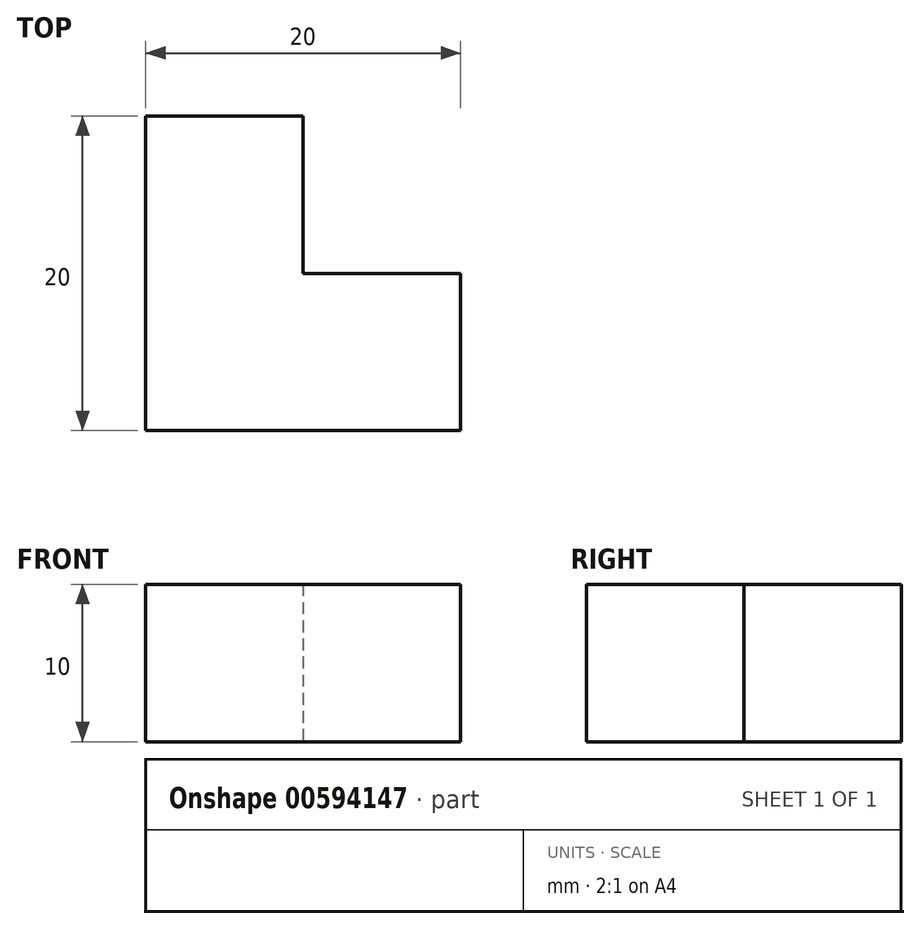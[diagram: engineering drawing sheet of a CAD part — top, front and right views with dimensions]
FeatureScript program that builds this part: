
annotation { "Feature Type Name" : "Feature", "Feature Type Description" : "" }
export const myFeature = defineFeature(function(context is Context, id is Id, definition is map)
    precondition{}
    {
        {
            var Q0;
            Q0=qCreatedBy(makeId("Top.planeOp"),FACE);
            var sketch = newSketch(context, id + "F0", { "sketchPlane" : qUnion([Q0])});
            skLineSegment(sketch, "E0", {"start": v(0, 0) * mm, "end": v(0, 20) * mm});
            skLineSegment(sketch, "E1", {"start": v(0, 20) * mm, "end": v(10, 20) * mm});
            skLineSegment(sketch, "E2", {"start": v(10, 20) * mm, "end": v(10, 10) * mm});
            skLineSegment(sketch, "E3", {"start": v(10, 10) * mm, "end": v(20, 10) * mm});
            skLineSegment(sketch, "E4", {"start": v(20, 10) * mm, "end": v(20, 0) * mm});
            skLineSegment(sketch, "E5", {"start": v(20, 0) * mm, "end": v(0, 0) * mm});
            skSolve(sketch);
        }
        {
            var Q0;
            Q0 = qSketchRegion(id + "F0", true);
            extrude(context, id + "F1", {"entities" : qUnion([Q0]), "depth" : 10 * mm, "offsetDistance" : 25 * mm});
        }
    });
